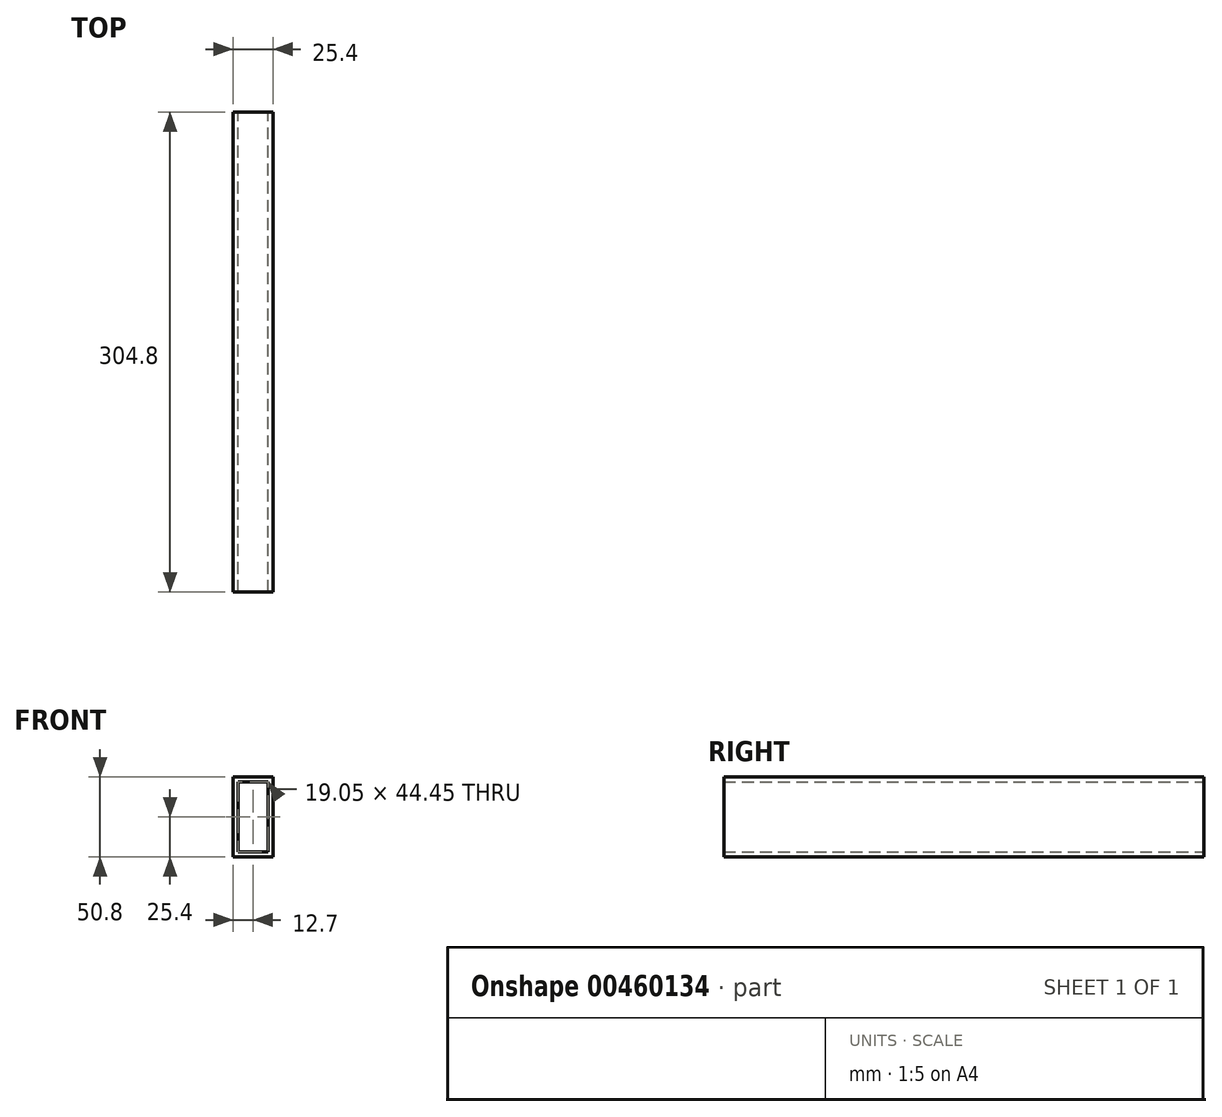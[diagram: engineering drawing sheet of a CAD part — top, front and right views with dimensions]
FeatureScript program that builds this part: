
annotation { "Feature Type Name" : "Feature", "Feature Type Description" : "" }
export const myFeature = defineFeature(function(context is Context, id is Id, definition is map)
    precondition{}
    {
        {
            var Q0;
            Q0=qCreatedBy(makeId("Front.planeOp"),FACE);
            var sketch = newSketch(context, id + "F0", { "sketchPlane" : qUnion([Q0])});
            skLineSegment(sketch, "E0.bottom", {"start": v(12.7, 25.4) * mm, "end": v(-12.7, 25.4) * mm});
            skLineSegment(sketch, "E0.top", {"start": v(12.7, -25.4) * mm, "end": v(-12.7, -25.4) * mm});
            skLineSegment(sketch, "E0.left", {"start": v(12.7, 25.4) * mm, "end": v(12.7, -25.4) * mm});
            skLineSegment(sketch, "E0.right", {"start": v(-12.7, 25.4) * mm, "end": v(-12.7, -25.4) * mm});
            skPoint(sketch, "E0.middle", {"position": v(0, 0) * mm});
            skLineSegment(sketch, "E1.bottom", {"start": v(9.53, 22.23) * mm, "end": v(-9.52, 22.23) * mm});
            skLineSegment(sketch, "E1.top", {"start": v(9.53, -22.23) * mm, "end": v(-9.52, -22.23) * mm});
            skLineSegment(sketch, "E1.left", {"start": v(9.53, 22.23) * mm, "end": v(9.53, -22.23) * mm});
            skLineSegment(sketch, "E1.right", {"start": v(-9.52, 22.23) * mm, "end": v(-9.52, -22.23) * mm});
            skSolve(sketch);
        }
        {
            var Q0;
            Q0=makeQuery(id+"F0.imprint","IMPRINT",FACE,{"disambiguationData":[TD([[makeQuery(id+"F0.imprint","IMPRINT",EDGE,{"derivedFrom":sQuery(id+"F0.wireOp",EDGE,"E0.bottom")}),1.0]])]});
            extrude(context, id + "F1", {"entities" : qUnion([Q0]), "depth" : 304.8 * mm});
        }
    });
